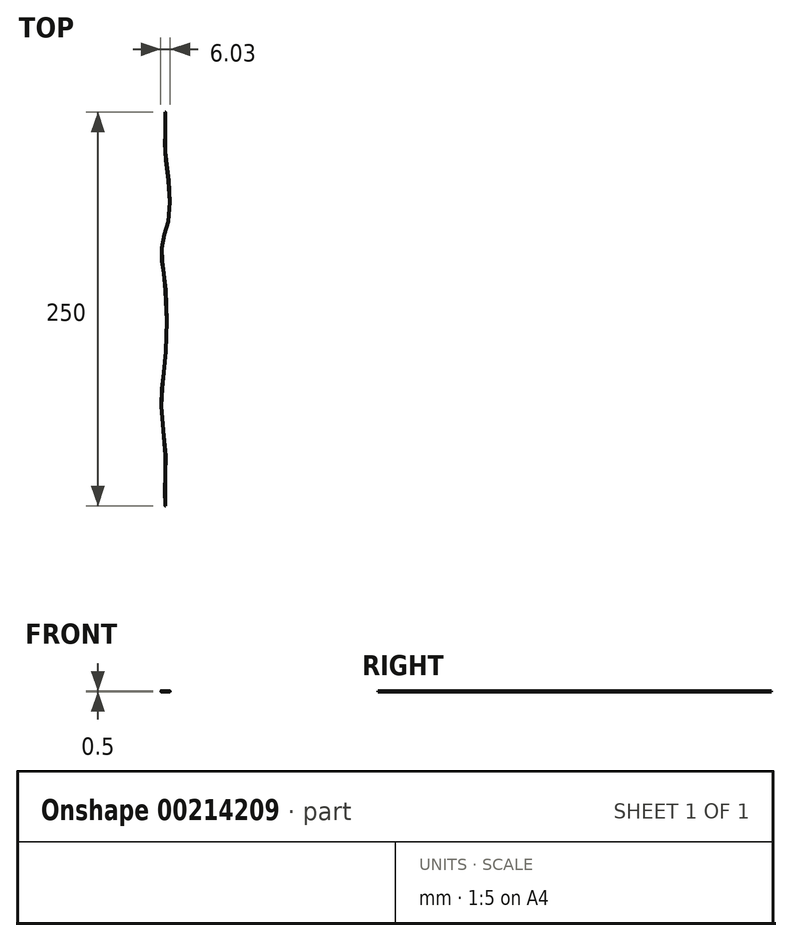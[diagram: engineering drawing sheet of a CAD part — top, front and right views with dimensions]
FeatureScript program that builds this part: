
annotation { "Feature Type Name" : "Feature", "Feature Type Description" : "" }
export const myFeature = defineFeature(function(context is Context, id is Id, definition is map)
    precondition{}
    {
        {
            var Q0;
            Q0=qCreatedBy(makeId("Front.planeOp"),FACE);
            var sketch = newSketch(context, id + "F0", { "sketchPlane" : qUnion([Q0])});
            skCircle(sketch, "E0", {"center": v(0, 0) * mm, "radius": 0.25 * mm});
            skSolve(sketch);
        }
        {
            var Q0;
            Q0=qCreatedBy(makeId("Top.planeOp"),FACE);
            var sketch = newSketch(context, id + "F1", { "sketchPlane" : qUnion([Q0])});
            skFitSpline(sketch, "E1", {"points": [v(0, 0) * mm, v(0, -15.9) * mm, v(0, -23.46) * mm, v(1.68, -39.9) * mm, v(2.74, -64.3) * mm, v(0, -75.79) * mm, v(-2.33, -88.45) * mm, v(0, -109.57) * mm, v(0, -157.37) * mm, v(-2.56, -184.8) * mm, v(0, -214.95) * mm, v(0, -233.58) * mm, v(0, -250) * mm], "startDerivative": vector(2.9, -241.32) * mm, "endDerivative": vector(-0.74, -216.35) * mm});
            skLineSegment(sketch, "E2", {"start": v(0, 0) * mm, "end": v(0, -250) * mm, "construction": true});
            skSolve(sketch);
        }
        {
            var Q0;
            Q0 = qSketchRegion(id + "F0", true);
            var Q1;
            Q1 = qConstructionFilter(qBodyType(qCreatedBy(id + "F1" ,EDGE), BodyType.WIRE), ConstructionObject.NO);
            sweep(context, id + "F2", {"profiles" : qUnion([Q0]), "path" : qUnion([Q1])});
        }
    });
